# Revit family: NBS_GreshamOfficeFurnitureLtd_OffcChrs_Klyro-Pouf
name_source: partatom
category: Furniture
units: mm (PartAtom-declared; Revit-internal decimal feet)

## family parameters
Always vertical = Yes
Cut with Voids When Loaded = No
Room Calculation Point = No
Shared = No
Work Plane-Based = No

## types (3) — shared parameters
AssetType = Fixed
Category = Pr_40_50_12_57:Office chairs
DurationUnit = year
IfcExportAs = IfcFurnitureType
IfcExportType = CHAIR
IsBuiltIn = No
ManufacturerName = Gresham Office Furniture Ltd
ManufacturerURL = www.gof.co.uk
NBSCertification = www.nationalbimlibrary.com/cert/01qzvfss
NBSDescription = Office chairs
NBSReference = 45-35-20/330
NominalDepth = 550 mm
NominalHeight = 410 mm
NominalLength = 550 mm
Recyclability = 100%
SeatsAndBacksMaterial = To BS EN 16139:2013+AC2013 Level 2
Size = 410 x 550 x 550 mm
StandardsDurability = To BS EN 16139:2013+AC2013 Level 2
Status = UNSET
Uniclass2015Code = Pr_40_50_12_57
Uniclass2015Title = Office chairs
Uniclass2015Version = Products v1.23
Version = 1
WarrantyDescription = Five year
WarrantyDurationUnit = year
zero-valued in all types: HighestSeatingHeight, LowestSeatingHeight, NominalWidth, SeatingHeight

## per-type parameters (varying)
| type | 4LegBase | BIMObjectName | BaseColour | BaseType | Material | ModelReference | Name | SeatHeight | Weight | Wooden4LegBase | WoodenPyramidSwivelBase |
| 4LegBase_KLYP1 | Yes | NBS_GreshamOfficeFurnitureLtd_OfficeChairs_Klyro-Pouf_KLYP1 | Dark walnut; Natural | Four legged base | Polyurethane, Wood, Fabric | KLYP1 | OfficeChairs_Klyro-Pouf_KLYP1_GreshamOfficeFurnitureLtd | 338 mm | 12.7 Kg | No | No |
| WoodenPyramidSwivelBase_KLYP2 | No | NBS_GreshamOfficeFurnitureLtd_OfficeChairs_Klyro-Pouf_KLYP2 | Dark walnut; Natural | Pyramid swivel base | Polyurethane, Wood, Fabric | KLYP2 | OfficeChairs_Klyro-Pouf_KLYP2_GreshamOfficeFurnitureLtd | 331 mm  [stored 1.08596 ft] | 9.7 Kg | No | Yes |
| Wooden4LegBase_KLYP5 | No | NBS_GreshamOfficeFurnitureLtd_OfficeChairs_Klyro-Pouf_KLYP5 | Black; Grey; Silver; White; Chrome | Four star swivel base | Polyurethane, Metal, Fabric | KLYP5 | OfficeChairs_Klyro-Pouf_KLYP5_GreshamOfficeFurnitureLtd | 353 mm | 7.7 Kg | Yes | No |

note: [stored X ft] marks values corroborated as IEEE doubles in the binary element streams (Revit-internal decimal feet)

## geometry (parser evidence)
native form markers: Sweep x18
no freeform markers — native parametric forms only
